# Revit family: xBall_Valve-Full_Port-WATTS-S-FBV-1_Series
name_source: partatom
category: Pipe Accessories
units: mm (PartAtom-declared; Revit-internal decimal feet)

## family parameters
Always vertical = Yes
Cut with Voids When Loaded = No
OmniClass Number = 23.65.55.14
OmniClass Title = Valves for Liquid Services
Part Type = Valve - Breaks Into
Round Connector Dimension = Use Diameter
Shared = Yes
Work Plane-Based = No

## types (10) — shared parameters
Assembly Code = D2090900
Country = United States
Default Elevation = 0"
Finish = Metal-WATTS-Stainless Steel
Finish- Handle = Plastic-WATTS-Yellow
Manufacturer = WATTS
Manufacturer Product Line = Ball Valves
Material = Metal-WATTS-Stainless Steel
Max. Working Pressure = 1000psi (69 bar) WOG non-shock; 125psi (8.6 bar) WSP
Model = S-FBV-1
Price = Prices may vary. Please consult Manufacturer Representative for most up-to-date price list.
Product Documentation Link = https://www.watts.com
Product Page URL = https://www.watts.com
Region = North America
Temperature Range = 0˚F - 400˚F (-18˚C – 204˚C)
URL = http://www.watts.com

## per-type parameters (varying)
| type | C | C1 - Stem Top | C2 - Bottom of Stem Flat | C3 - Mounting Pad to Stem Top | C4 - Stem Flat Height | Connection Diameter | Description | E - Center to End | H - Radius to Handle | Hex | J - Ball Orifice | K1 - Stem Diameter | L - End to End | W | W1 | W2 | Weight Lbs |
| S-FBV-1 1/4" | 1 3/4" | 1 9/16" | 1" | 7/8" | 9/16" | 1/4" | 1/4 In 2-Piece Full Port StaInless Steel Ball Valve, NPT Threaded End Connection, Latch-Lok Handle | 1 1/16" | 3 15/16" | 1 1/8" | 1/4" | 5/16" | 2 1/16" | 1 1/8" | 1/2" | 3/16" | .68 |
| S-FBV-1 3/8" | 1 3/4" | 1 9/16" | 1" | 7/8" | 9/16" | 3/8" | 3/8 In 2-Piece Full Port StaInless Steel Ball Valve, NPT Threaded End Connection, Latch-Lok Handle | 1 1/16" | 3 15/16" | 1 1/8" | 3/8" | 5/16" | 2 1/16" | 1 1/8" | 1/2" | 3/16" | .68 |
| S-FBV-1 1/2" | 2" | 1 3/4" | 1 3/16" | 1 1/8" | 9/16" | 1/2" | 1/2 In 2-Piece Full Port StaInless Steel Ball Valve, NPT Threaded End Connection, Latch-Lok Handle | 1 3/16" | 4 1/2" | 1 1/8" | 1/2" | 3/8" | 2 3/8" | 1 1/8" | 1/2" | 1/4" | .9 |
| S-FBV-1 3/4" | 2" | 2" | 1 3/8" | 1 1/8" | 9/16" | 3/4" | 3/4 In 2-Piece Full Port StaInless Steel Ball Valve, NPT Threaded End Connection, Latch-Lok Handle | 1 5/16" | 4 1/2" | 1 3/8" | 3/4" | 3/8" | 2 5/8" | 1 3/8" | 7/8" | 1/4" | 1.39 |
| S-FBV-1 1" | 2 1/2" | 2 1/4" | 1 11/16" | 1 5/16" | 5/8" | 1" | 1 In 2-Piece Full Port StaInless Steel Ball Valve, NPT Threaded End Connection, Latch-Lok Handle | 1 5/8" | 4 15/16" | 1 3/8" | 1" | 7/16" | 3 1/4" | 1 3/8" | 7/8" | 5/16" | 1.98 |
| S-FBV-1 1-1/4" | 2 3/4" | 2 1/2" | 1 7/8" | 1 5/16" | 5/8" | 1 1/4" | 1-1/4 In 2-Piece Full Port StaInless Steel Ball Valve, NPT Threaded End Connection, Latch-Lok Handle | 1 3/4" | 4 15/16" | 1 1/2" | 1 1/4" | 7/16" | 3 5/8" | 1 1/2" | 15/16" | 5/16" | 3.21 |
| S-FBV-1 1-1/2" | 3 5/16" | 3" | 2 1/8" | 1 9/16" | 7/8" | 1 1/2" | 1-1/2 In 2-Piece Full Port StaInless Steel Ball Valve, NPT Threaded End Connection, Latch-Lok Handle | 2 1/4" | 6 5/16" | 2 1/4" | 1 1/2" | 5/8" | 4 3/8" | 1 1/2" | 15/16" | 3/8" | 4.50 |
| S-FBV-1 2" | 3 5/8" | 3 1/4" | 2 1/2" | 1 5/8" | 3/4" | 2" | 2 In 2-Piece Full Port StaInless Steel Ball Valve, NPT Threaded End Connection, Latch-Lok Handle | 2 1/2" | 6 5/16" | 2 1/4" | 2" | 5/8" | 4 15/16" | 1 1/2" | 15/16" | 3/8" | 7.17 |
| S-FBV-1 2-1/2" | 4 1/2" | 4 1/2" | 3 5/16" | 2 1/8" | 1 1/4" | 2 1/2" | 2-1/2 In 2-Piece Full Port StaInless Steel Ball Valve, NPT Threaded End Connection, Latch-Lok Handle | 3 1/4" | 9 1/16" | 2 5/8" | 2 1/2" | 3/4" | 6 7/16" | 2 3/16" | 1 3/8" | 1/2" | 15.4 |
| S-FBV-1 3" | 5" | 4 15/16" | 3 3/4" | 2 1/8" | 1 3/16" | 3" | 3 In 2-Piece Full Port StaInless Steel Ball Valve, NPT Threaded End Connection, Latch-Lok Handle | 3 1/2" | 9 1/16" | 3 1/2" | 3" | 3/4" | 7 1/2" | 2 3/16" | 1 3/8" | 1/2" | 21.17 |

## geometry (parser evidence)
native form markers: Sweep x3
no freeform markers — native parametric forms only
